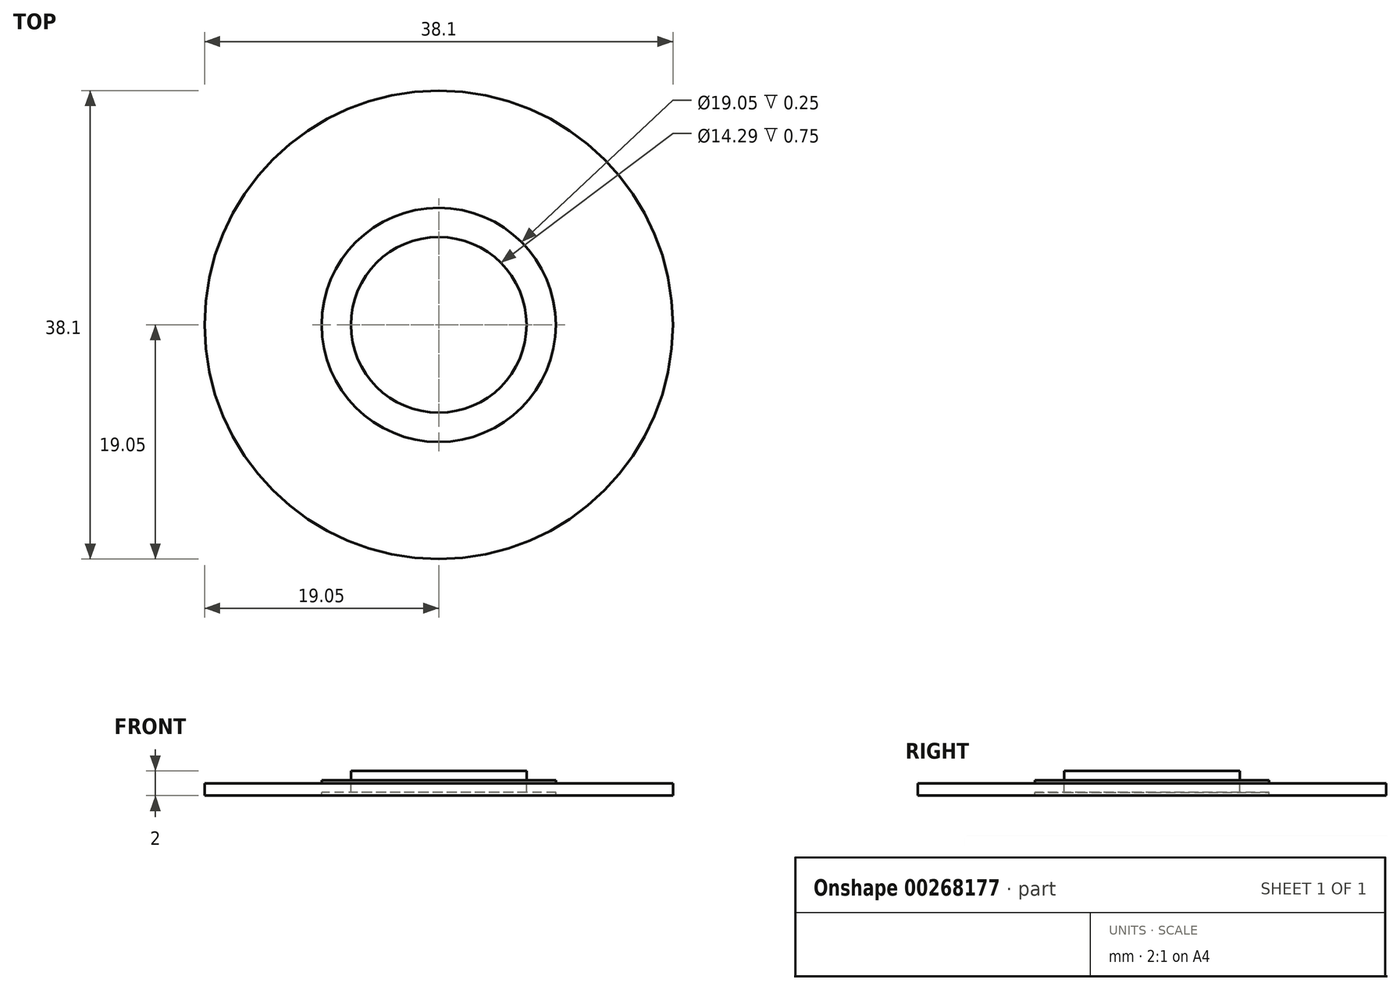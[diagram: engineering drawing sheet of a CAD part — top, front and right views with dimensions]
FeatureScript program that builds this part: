
annotation { "Feature Type Name" : "Feature", "Feature Type Description" : "" }
export const myFeature = defineFeature(function(context is Context, id is Id, definition is map)
    precondition{}
    {
        {
            var Q0;
            Q0=qCreatedBy(makeId("Top.planeOp"),FACE);
            var sketch = newSketch(context, id + "F0", { "sketchPlane" : qUnion([Q0])});
            skCircle(sketch, "E0", {"center": v(0, 0) * mm, "radius": 19.05 * mm});
            skCircle(sketch, "E1", {"center": v(0, 0) * mm, "radius": 9.53 * mm});
            skCircle(sketch, "E2", {"center": v(0, 0) * mm, "radius": 7.14 * mm});
            skSolve(sketch);
        }
        {
            var Q0;
            Q0 = qSketchRegion(id + "F0", true);
            extrude(context, id + "F1", {"entities" : qUnion([Q0]), "oppositeDirection" : true, "depth" : 1 * mm});
        }
        {
            var Q0;
            Q0=makeQuery(id+"F0.imprint","IMPRINT",FACE,{"disambiguationData":[TD([[makeQuery(id+"F0.imprint","IMPRINT",EDGE,{"derivedFrom":sQuery(id+"F0.wireOp",EDGE,"E1")}),1.0]])]});
            extrude(context, id + "F2", {"entities" : qUnion([Q0]), "depth" : .25 * mm});
        }
        {
            var Q0;
            Q0=makeQuery(id+"F0.imprint","IMPRINT",FACE,{"disambiguationData":[TD([[makeQuery(id+"F0.imprint","IMPRINT",EDGE,{"derivedFrom":sQuery(id+"F0.wireOp",EDGE,"E2")}),1.0]])]});
            extrude(context, id + "F3", {"entities" : qUnion([Q0]), "operationType" : NewBodyOperationType.ADD, "depth" : 1 * mm});
        }
        {
            var Q0;
            Q0=makeQuery(id+"F0.imprint","IMPRINT",FACE,{"disambiguationData":[TD([[makeQuery(id+"F0.imprint","IMPRINT",EDGE,{"derivedFrom":sQuery(id+"F0.wireOp",EDGE,"E1")}),1.0]])]});
            extrude(context, id + "F4", {"entities" : qUnion([Q0]), "operationType" : NewBodyOperationType.ADD, "oppositeDirection" : true, "depth" : .75 * mm});
        }
        {
            var Q0;
            Q0=makeQuery(id+"F1.opExtrude","SWEPT_BODY",BODY,{"disambiguationData":[OSD([sQuery(id+"F0.wireOp",EDGE,"E0"),sQuery(id+"F0.wireOp",EDGE,"E1")])]});
            transform(context, id + "F5", {"entities" : qUnion([Q0]), "transformType" : TransformType.TRANSLATION_3D, "dx" : 0 * mm, "dy" : 0 * mm, "dz" : -6.35 * mm, "makeCopy" : true});
        }
        {
            var Q0;
            Q0=makeQuery(id+"F5.opPattern","COPY",BODY,{"derivedFrom":makeQuery(id+"F1.opExtrude","SWEPT_BODY",BODY,{"disambiguationData":[OSD([sQuery(id+"F0.wireOp",EDGE,"E0"),sQuery(id+"F0.wireOp",EDGE,"E1")])]}),"instanceName":"1"});
            deleteBodies(context, id + "F6", {"entities" : qUnion([Q0])});
        }
    });
